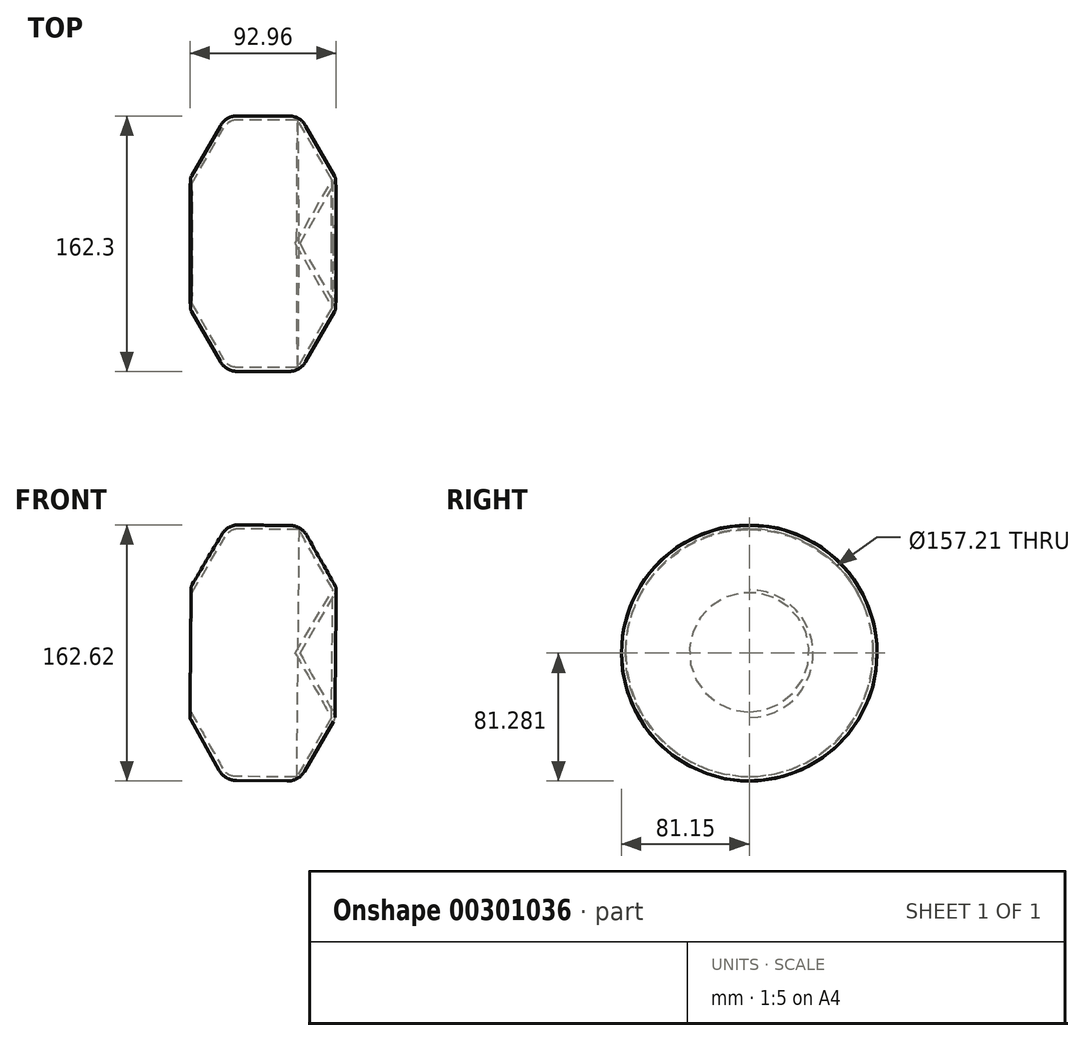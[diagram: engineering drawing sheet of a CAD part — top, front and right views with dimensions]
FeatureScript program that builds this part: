
annotation { "Feature Type Name" : "Feature", "Feature Type Description" : "" }
export const myFeature = defineFeature(function(context is Context, id is Id, definition is map)
    precondition{}
    {
        {
            var Q0;
            Q0=qCreatedBy(makeId("Front.planeOp"),FACE);
            var sketch = newSketch(context, id + "F0", { "sketchPlane" : qUnion([Q0])});
            skCircle(sketch, "E0.cCircle", {"center": v(0, 0) * mm, "radius": 40.57 * mm, "construction": true});
            skLineSegment(sketch, "E0.0", {"start": v(23.84, 40.33) * mm, "end": v(46.85, -0.48) * mm});
            skLineSegment(sketch, "E0.1", {"start": v(46.85, -0.48) * mm, "end": v(23, -40.81) * mm});
            skLineSegment(sketch, "E0.2", {"start": v(23, -40.81) * mm, "end": v(-23.84, -40.33) * mm});
            skLineSegment(sketch, "E0.3", {"start": v(-23.84, -40.33) * mm, "end": v(-46.85, 0.48) * mm});
            skLineSegment(sketch, "E0.4", {"start": v(-46.85, 0.48) * mm, "end": v(-23, 40.81) * mm});
            skLineSegment(sketch, "E0.5", {"start": v(-23, 40.81) * mm, "end": v(23.84, 40.33) * mm});
            skPoint(sketch, "E0.0.midPoint", {"position": v(35.35, 19.92) * mm});
            skSolve(sketch);
        }
        {
            var Q0;
            Q0=makeQuery(id+"F0.imprint","IMPRINT",FACE,{"disambiguationData":[TD([[makeQuery(id+"F0.imprint","IMPRINT",EDGE,{"derivedFrom":sQuery(id+"F0.wireOp",EDGE,"E0.0")}),-1.0]])]});
            var Q1;
            Q1=sQuery(id+"F0.wireOp",EDGE,"E0.5");
            revolve(context, id + "F1", {"entities" : qUnion([Q0]), "axis" : qUnion([Q1]), "revolveType" : RevolveType.FULL});
        }
        {
            var Q0;
            Q0=makeQuery(id+"F1.opRevolve","SWEPT_EDGE",EDGE,{"disambiguationData":[OSD([sQuery(id+"F0.wireOp",EDGE,"E0.2"),sQuery(id+"F0.wireOp",EDGE,"E0.3")])]});
            fillet(context, id + "F2", {"entities" : qUnion([Q0]), "radius" : 12.7 * mm, "tangentPropagation" : true, "rho" : 0.5, "crossSection" : FilletCrossSection.CONIC, "allowEdgeOverflow" : false});
        }
        {
            var Q0;
            Q0=makeQuery(id+"F1.opRevolve","SWEPT_FACE",FACE,{"disambiguationData":[OSD([sQuery(id+"F0.wireOp",EDGE,"E0.4")])]});
            shell(context, id + "F3", {"entities" : qUnion([Q0]), "thickness" : 2.54 * mm});
        }
        {
            var Q0;
            Q0=makeQuery(id+"F1.opRevolve","SWEPT_EDGE",EDGE,{"disambiguationData":[OSD([sQuery(id+"F0.wireOp",EDGE,"E0.1"),sQuery(id+"F0.wireOp",EDGE,"E0.2")])]});
            fillet(context, id + "F4", {"entities" : qUnion([Q0]), "radius" : 12.7 * mm, "tangentPropagation" : true, "rho" : 0.5, "crossSection" : FilletCrossSection.CONIC, "allowEdgeOverflow" : false});
        }
        {
            var Q0;
            Q0=makeQuery(id+"F1.opRevolve","SWEPT_EDGE",EDGE,{"disambiguationData":[OSD([sQuery(id+"F0.wireOp",EDGE,"E0.0"),sQuery(id+"F0.wireOp",EDGE,"E0.1")])]});
            fillet(context, id + "F5", {"entities" : qUnion([Q0]), "radius" : 5.08 * mm, "tangentPropagation" : true, "allowEdgeOverflow" : false});
        }
        {
            var Q0;
            Q0=makeQuery(id+"F1.opRevolve","SWEPT_EDGE",EDGE,{"disambiguationData":[OSD([sQuery(id+"F0.wireOp",EDGE,"E0.3"),sQuery(id+"F0.wireOp",EDGE,"E0.4")])]});
            fillet(context, id + "F6", {"entities" : qUnion([Q0]), "radius" : 5.08 * mm, "tangentPropagation" : true, "allowEdgeOverflow" : false});
        }
    });
